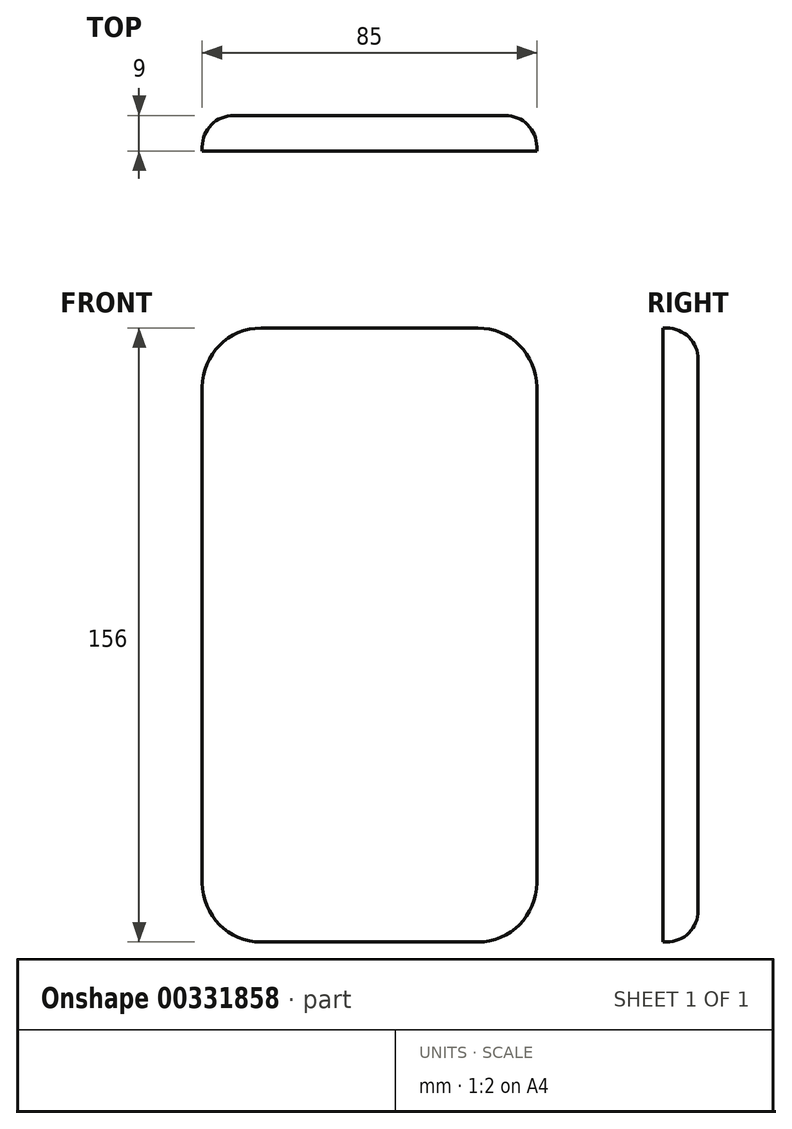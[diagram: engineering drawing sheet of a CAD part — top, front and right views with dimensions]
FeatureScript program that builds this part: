
annotation { "Feature Type Name" : "Feature", "Feature Type Description" : "" }
export const myFeature = defineFeature(function(context is Context, id is Id, definition is map)
    precondition{}
    {
        {
            var Q0;
            Q0=qCreatedBy(makeId("Front.planeOp"),FACE);
            var sketch = newSketch(context, id + "F0", { "sketchPlane" : qUnion([Q0])});
            skLineSegment(sketch, "E0.rect.bottom", {"start": v(-27.5, -78) * mm, "end": v(27.5, -78) * mm});
            skLineSegment(sketch, "E0.rect.top", {"start": v(-27.5, 78) * mm, "end": v(27.5, 78) * mm});
            skLineSegment(sketch, "E0.rect.left", {"start": v(-42.5, -63) * mm, "end": v(-42.5, 63) * mm});
            skLineSegment(sketch, "E0.rect.right", {"start": v(42.5, -63) * mm, "end": v(42.5, 63) * mm});
            skPoint(sketch, "E0.rect.middle", {"position": v(0, 0) * mm});
            skPoint(sketch, "E1.visualSharp", {"position": v(-42.5, 78) * mm});
            skArc(sketch, "E1.filletArc", {"start": v(-27.5, 78) * mm, "mid": v(-38.1, 73.6) * mm, "end": v(-42.5, 63) * mm});
            skPoint(sketch, "E2.visualSharp", {"position": v(42.5, 78) * mm});
            skArc(sketch, "E2.filletArc", {"start": v(42.5, 63) * mm, "mid": v(38.1, 73.6) * mm, "end": v(27.5, 78) * mm});
            skPoint(sketch, "E3.visualSharp", {"position": v(42.5, -78) * mm});
            skArc(sketch, "E3.filletArc", {"start": v(27.5, -78) * mm, "mid": v(38.1, -73.6) * mm, "end": v(42.5, -63) * mm});
            skPoint(sketch, "E4.visualSharp", {"position": v(-42.5, -78) * mm});
            skArc(sketch, "E4.filletArc", {"start": v(-42.5, -63) * mm, "mid": v(-38.1, -73.6) * mm, "end": v(-27.5, -78) * mm});
            skSolve(sketch);
        }
        {
            var Q0;
            Q0=qSketchRegion(id+"F0",true);
            extrude(context, id + "F1", {"entities" : qUnion([Q0]), "depth" : 9 * mm});
        }
        {
            var Q0;
            Q0=makeQuery(id+"F1.opExtrude","CAP_FACE",FACE,{"disambiguationData":[OSD([sQuery(id+"F0.wireOp",EDGE,"E0.rect.bottom"),sQuery(id+"F0.wireOp",EDGE,"E0.rect.top"),sQuery(id+"F0.wireOp",EDGE,"E0.rect.left"),sQuery(id+"F0.wireOp",EDGE,"E0.rect.right"),sQuery(id+"F0.wireOp",EDGE,"E1.filletArc"),sQuery(id+"F0.wireOp",EDGE,"E2.filletArc"),sQuery(id+"F0.wireOp",EDGE,"E3.filletArc"),sQuery(id+"F0.wireOp",EDGE,"E4.filletArc")])],"isStart":true});
            fillet(context, id + "F2", {"entities" : qUnion([Q0]), "radius" : 8 * mm, "tangentPropagation" : true, "allowEdgeOverflow" : false});
        }
    });
